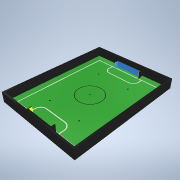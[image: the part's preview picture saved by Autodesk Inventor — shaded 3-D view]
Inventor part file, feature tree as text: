
AUTODESK INVENTOR PART (.ipt)
format: ipt  version: 2020 (Build 240168000, 168)  size: 389,632 bytes
history: native  units: mm
features: projected_geometry x16, extrude x7, sketch x6, other x1
ambient origin geometry x8: Origin, YZ Plane, XZ Plane, XY Plane, X Axis, Y Axis, Z Axis, Center Point
bodies: Body1 (feature_tree)
feature tree (30):
  other  "Твердое тело1"
  sketch  "Эскиз1"
  extrude  "Выдавливание1"  Depth=2430.0mm
  extrude  "Выдавливание2"  Depth=1820.0mm
  extrude  "Выдавливание3"  Depth=40.0mm
  extrude  "Выдавливание4"  Depth=40.0mm
  extrude  "Выдавливание5"  Depth=220.0mm TaperAngle=0.0deg
  extrude  "Выдавливание6"  Depth=5.0mm TaperAngle=0.0deg
  extrude  "Выдавливание7"  Depth=100.0mm
  sketch  "Эскиз2"
  projected_geometry  "Спроецированная петля1"
  projected_geometry  "Спроецированная петля2"
  sketch  "Эскиз3"
  projected_geometry  "Спроецированная петля3"
  sketch  "Эскиз4"
  projected_geometry  "Спроецированная петля4"
  projected_geometry  "Спроецированная петля5"
  projected_geometry  "Спроецированная петля6"
  projected_geometry  "Спроецированная петля7"
  projected_geometry  "Спроецированная петля8"
  sketch  "Эскиз5"
  projected_geometry  "Спроецированная петля9"
  projected_geometry  "Спроецированная петля10"
  sketch  "Эскиз6"
  projected_geometry  "Спроецированная петля11"
  projected_geometry  "Спроецированная петля12"
  projected_geometry  "Спроецированная петля13"
  projected_geometry  "Спроецированная петля14"
  projected_geometry  "Спроецированная петля15"
  projected_geometry  "Спроецированная петля16"
